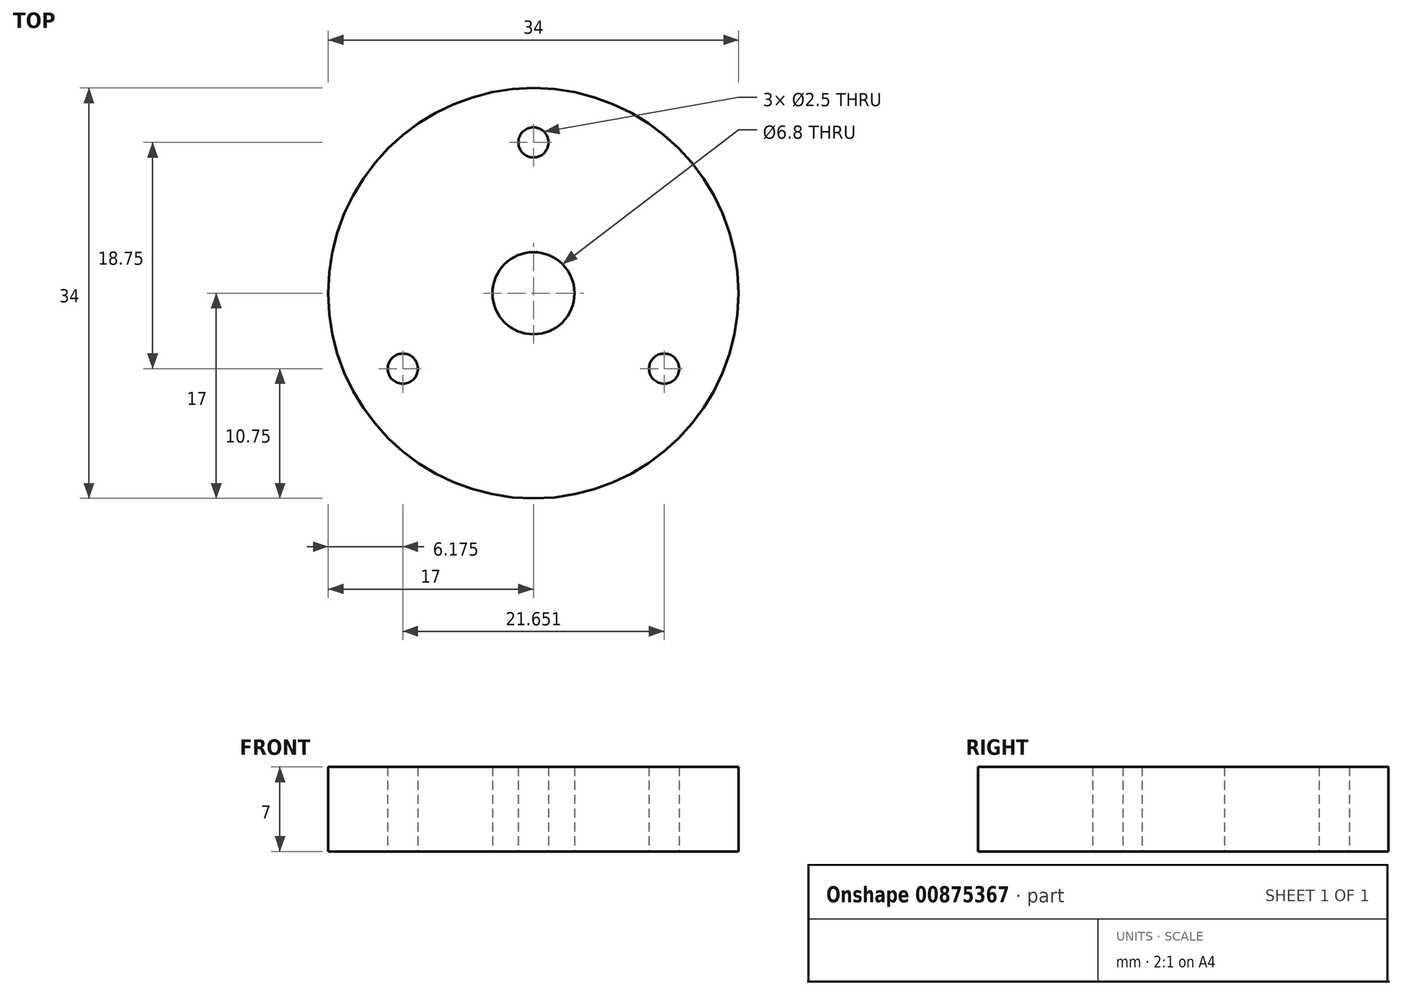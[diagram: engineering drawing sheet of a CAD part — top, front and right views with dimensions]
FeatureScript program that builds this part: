
annotation { "Feature Type Name" : "Feature", "Feature Type Description" : "" }
export const myFeature = defineFeature(function(context is Context, id is Id, definition is map)
    precondition{}
    {
        {
            var Q0;
            Q0=qCreatedBy(makeId("Top.planeOp"),FACE);
            var sketch = newSketch(context, id + "F0", { "sketchPlane" : qUnion([Q0])});
            skCircle(sketch, "E0", {"center": v(0, 0) * mm, "radius": 17 * mm});
            skSolve(sketch);
        }
        {
            var Q0;
            Q0=makeQuery(id+"F0.imprint","IMPRINT",FACE,{"disambiguationData":[TD([[makeQuery(id+"F0.imprint","IMPRINT",EDGE,{"derivedFrom":sQuery(id+"F0.wireOp",EDGE,"E0")}),1.0]])]});
            extrude(context, id + "F1", {"entities" : qUnion([Q0]), "depth" : 7 * mm, "offsetDistance" : 25 * mm});
        }
        {
            var Q0;
            Q0=makeQuery(id+"F1.opExtrude","CAP_FACE",FACE,{"disambiguationData":[OSD([sQuery(id+"F0.wireOp",EDGE,"E0")])],"isStart":false});
            var sketch = newSketch(context, id + "F2", { "sketchPlane" : qUnion([Q0])});
            skCircle(sketch, "E1", {"center": v(0, 0) * mm, "radius": 12.5 * mm, "construction": true});
            skPoint(sketch, "E2", {"position": v(0, 12.5) * mm});
            skPoint(sketch, "E3.1.0", {"position": v(-10.83, -6.25) * mm});
            skPoint(sketch, "E3.2.0", {"position": v(10.83, -6.25) * mm});
            skSolve(sketch);
        }
        {
            var Q0;
            Q0=sQuery(id+"F2.wireOp",VERTEX,"E1.center");
            var Q1;
            Q1=makeQuery(id+"F1.opExtrude","SWEPT_BODY",BODY,{"disambiguationData":[OSD([sQuery(id+"F0.wireOp",EDGE,"E0")])]});
            hole(context, id + "F3", {"style" : HoleStyle.SIMPLE, "endStyle" : HoleEndStyle.THROUGH, "standardTappedOrClearance" : lookupTablePath({ "standard" : "ISO", "engagement" : "75%", "pitch" : "1.25 mm", "size" : "M8", "type" : "Tapped" }), "standardBlindInLast" : lookupTablePath({ "standard" : "ISO", "fit" : "Normal", "engagement" : "75%", "pitch" : "1.25 mm", "size" : "M8", "type" : "Clearance & tapped" }), "holeDiameter" : 6.8 * mm, "majorDiameter" : 8 * mm, "showTappedDepth" : true, "isTappedThrough" : true, "tappedDepth" : 12 * mm, "tapClearance" : 3, "locations" : qUnion([Q0]), "scope" : qUnion([Q1]), "startStyle" : HoleStartStyle.SKETCH});
        }
        {
            var Q0;
            Q0=sQuery(id+"F2.wireOp",VERTEX,"E2");
            var Q1;
            Q1=sQuery(id+"F2.wireOp",VERTEX,"E3.2.0");
            var Q2;
            Q2=sQuery(id+"F2.wireOp",VERTEX,"E3.1.0");
            var Q3;
            Q3=makeQuery(id+"F1.opExtrude","SWEPT_BODY",BODY,{"disambiguationData":[OSD([sQuery(id+"F0.wireOp",EDGE,"E0")])]});
            hole(context, id + "F4", {"style" : HoleStyle.SIMPLE, "endStyle" : HoleEndStyle.THROUGH, "standardTappedOrClearance" : lookupTablePath({ "standard" : "ISO", "engagement" : "75%", "pitch" : "0.5 mm", "size" : "M3", "type" : "Tapped" }), "standardBlindInLast" : lookupTablePath({ "standard" : "ISO", "fit" : "Normal", "engagement" : "75%", "pitch" : "0.5 mm", "size" : "M3", "type" : "Clearance & tapped" }), "holeDiameter" : 2.5 * mm, "majorDiameter" : 3 * mm, "showTappedDepth" : true, "isTappedThrough" : true, "tappedDepth" : 12 * mm, "tapClearance" : 3, "locations" : qUnion([Q0, Q1, Q2]), "scope" : qUnion([Q3]), "startStyle" : HoleStartStyle.SKETCH});
        }
    });
